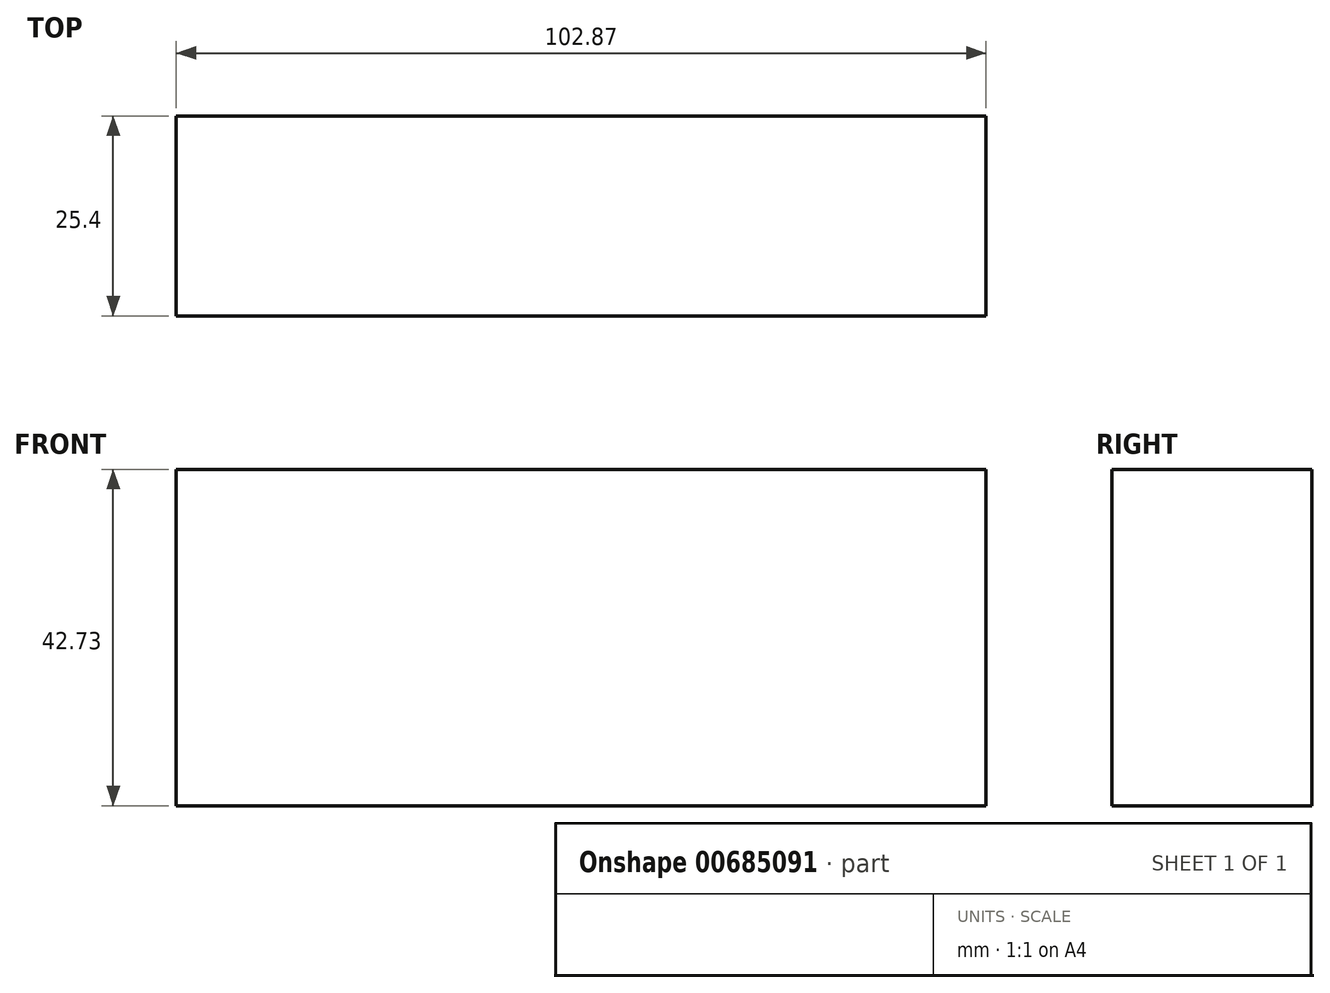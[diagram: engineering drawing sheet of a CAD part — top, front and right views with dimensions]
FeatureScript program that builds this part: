
annotation { "Feature Type Name" : "Feature", "Feature Type Description" : "" }
export const myFeature = defineFeature(function(context is Context, id is Id, definition is map)
    precondition{}
    {
        {
            var Q0;
            Q0=qCreatedBy(makeId("Front.planeOp"),FACE);
            var sketch = newSketch(context, id + "F0", { "sketchPlane" : qUnion([Q0])});
            skLineSegment(sketch, "E0.bottom", {"start": v(-55.29, 47.58) * mm, "end": v(47.58, 47.58) * mm});
            skLineSegment(sketch, "E0.top", {"start": v(-55.29, 4.85) * mm, "end": v(47.58, 4.85) * mm});
            skLineSegment(sketch, "E0.left", {"start": v(-55.29, 47.58) * mm, "end": v(-55.29, 4.85) * mm});
            skLineSegment(sketch, "E0.right", {"start": v(47.58, 47.58) * mm, "end": v(47.58, 4.85) * mm});
            skSolve(sketch);
        }
        {
            var Q0;
            Q0=makeQuery(id+"F0.imprint","IMPRINT",FACE,{"disambiguationData":[TD([[makeQuery(id+"F0.imprint","IMPRINT",EDGE,{"derivedFrom":sQuery(id+"F0.wireOp",EDGE,"E0.bottom")}),-1.0]])]});
            extrude(context, id + "F1", {"entities" : qUnion([Q0]), "depth" : 25.4 * mm, "offsetDistance" : 25.4 * mm});
        }
    });
